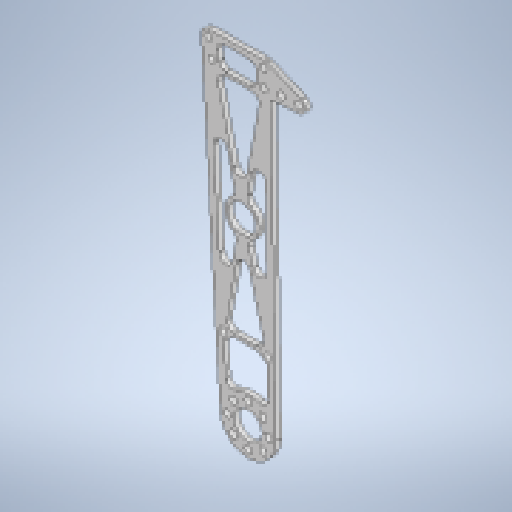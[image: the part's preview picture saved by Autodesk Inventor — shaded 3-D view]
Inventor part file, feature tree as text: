
AUTODESK INVENTOR PART (.ipt)
format: ipt  version: 2025.1 (Build 291241000, 241)  size: 351,744 bytes
history: native  units: mm
features: reference x13, other x9, extrude x3, fillet x3, sketch x3
ambient origin geometry x8: Origin, YZ Plane, XZ Plane, XY Plane, X Axis, Y Axis, Z Axis, Center Point
bodies: Body1 (feature_tree)
feature tree (31):
  other  "ソリッド1"
  extrude  "押し出し1"  Depth=8.0mm
  fillet  "フィレット1"  Radius=16.0mm
  extrude  "押し出し2"  Depth=12.0mm
  fillet  "フィレット2"  Radius=2.2mm
  extrude  "押し出し3"  Depth=80.0mm TaperAngle=360.0deg
  fillet  "フィレット3"  Radius=2.2mm
  sketch  "スケッチ1"
  reference  "参照1"
  other  "スケッチ円形状パターン1"
  reference  "参照2"
  reference  "参照3"
  reference  "参照4"
  reference  "参照5"
  reference  "参照6"
  reference  "参照7"
  reference  "参照8"
  reference  "参照9"
  reference  "参照10"
  reference  "参照11"
  reference  "参照12"
  sketch  "スケッチ2"
  sketch  "スケッチ3"
  reference  "参照13"
  other  "<userpath>\Documents\Inventor\Vixen\doutai.iam"
  other  "doutai.iam"
  other  "02157_SmallDiameterHornB_MIR1:1"
  other  "newnewude:3"
  other  "KRS2500_scale:15"
  other  "newnewude_2:1"
  other  "ude_tunagi:1"
